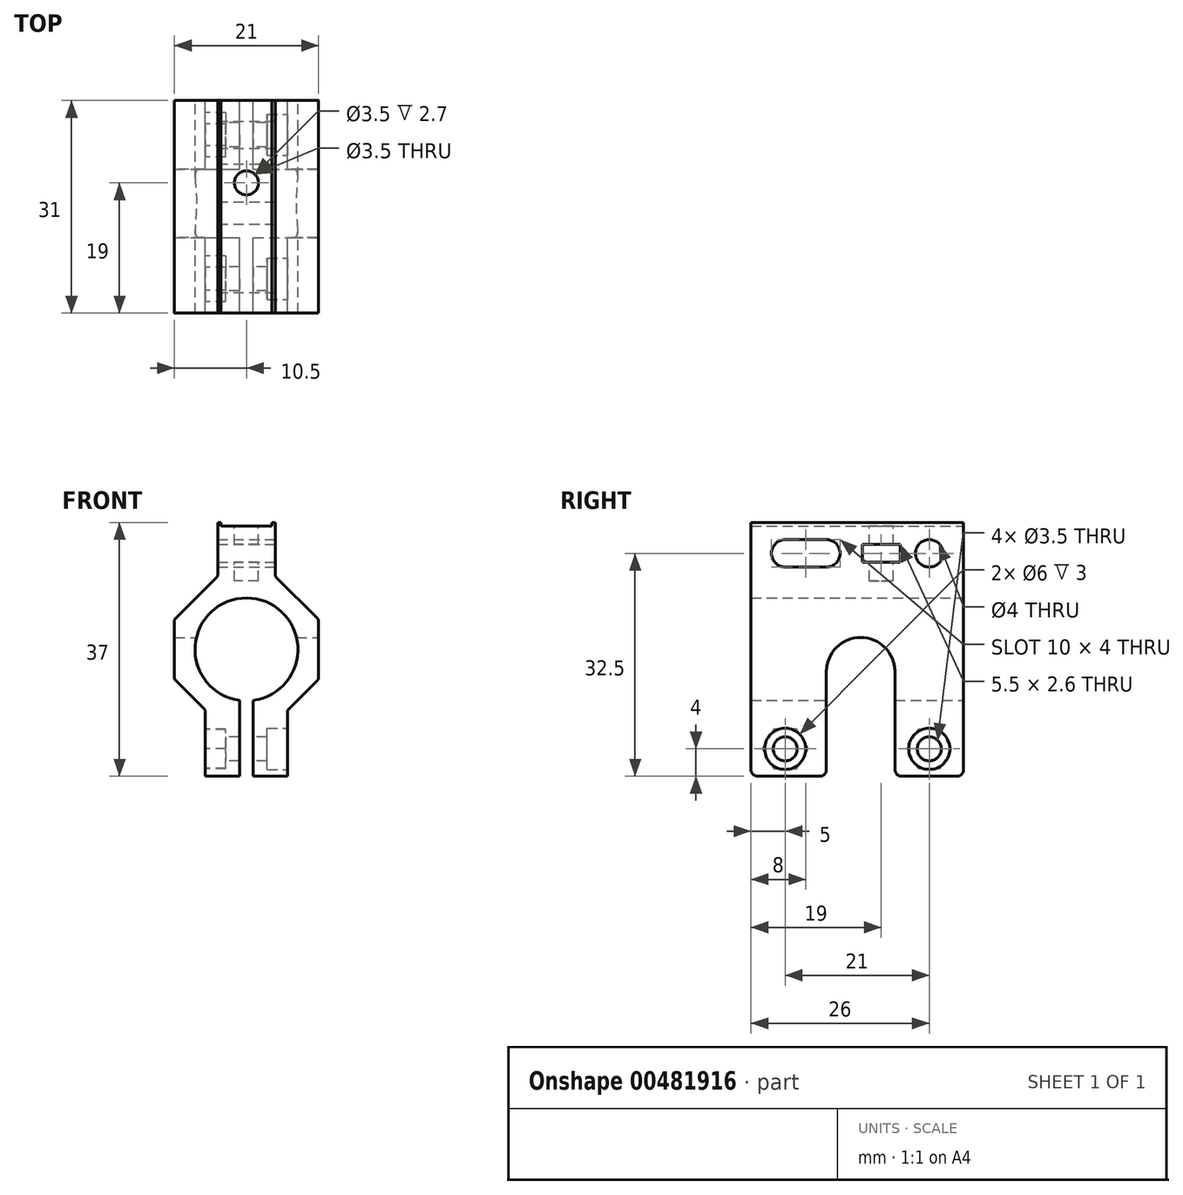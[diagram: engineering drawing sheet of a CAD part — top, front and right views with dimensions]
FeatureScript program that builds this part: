
annotation { "Feature Type Name" : "Feature", "Feature Type Description" : "" }
export const myFeature = defineFeature(function(context is Context, id is Id, definition is map)
    precondition{}
    {
        {
            var Q0;
            Q0=qCreatedBy(makeId("Front.planeOp"),FACE);
            var sketch = newSketch(context, id + "F0", { "sketchPlane" : qUnion([Q0])});
            skCircle(sketch, "E0", {"center": v(0, 0) * mm, "radius": 7.5 * mm});
            skCircle(sketch, "E1.cCircle", {"center": v(0, 0) * mm, "radius": 10.5 * mm, "construction": true});
            skLineSegment(sketch, "E1.1", {"start": v(4.2, 10.65) * mm, "end": v(10.5, 4.35) * mm});
            skLineSegment(sketch, "E1.2", {"start": v(10.5, 4.35) * mm, "end": v(10.5, -4.35) * mm});
            skLineSegment(sketch, "E1.3", {"start": v(10.5, -4.35) * mm, "end": v(6, -8.85) * mm});
            skLineSegment(sketch, "E1.5", {"start": v(-6, -8.85) * mm, "end": v(-10.5, -4.35) * mm});
            skLineSegment(sketch, "E1.6", {"start": v(-10.5, -4.35) * mm, "end": v(-10.5, 4.35) * mm});
            skLineSegment(sketch, "E1.7", {"start": v(-10.5, 4.35) * mm, "end": v(-4.2, 10.65) * mm});
            skPoint(sketch, "E1.0.midPoint", {"position": v(0, 10.5) * mm});
            skLineSegment(sketch, "E2.bottom", {"start": v(-3.7, 18) * mm, "end": v(3.7, 18) * mm});
            skLineSegment(sketch, "E2.left", {"start": v(-4.2, 18.5) * mm, "end": v(-4.2, 10.65) * mm});
            skLineSegment(sketch, "E2.right", {"start": v(4.2, 18.5) * mm, "end": v(4.2, 10.65) * mm});
            skLineSegment(sketch, "E3.top", {"start": v(-6, -18.5) * mm, "end": v(6, -18.5) * mm});
            skLineSegment(sketch, "E3.left", {"start": v(-6, -8.85) * mm, "end": v(-6, -18.5) * mm});
            skLineSegment(sketch, "E3.right", {"start": v(6, -8.85) * mm, "end": v(6, -18.5) * mm});
            skLineSegment(sketch, "E4", {"start": v(0, 0) * mm, "end": v(0, 19.36) * mm, "construction": true});
            skLineSegment(sketch, "E5", {"start": v(-3.7, 18) * mm, "end": v(-3.7, 18.5) * mm});
            skLineSegment(sketch, "E6", {"start": v(-3.7, 18.5) * mm, "end": v(-4.2, 18.5) * mm});
            skLineSegment(sketch, "E7", {"start": v(3.7, 18) * mm, "end": v(3.7, 18.5) * mm});
            skLineSegment(sketch, "E8", {"start": v(3.7, 18.5) * mm, "end": v(4.2, 18.5) * mm});
            skSolve(sketch);
        }
        {
            var Q0;
            Q0 = qSketchRegion(id + "F0", true);
            extrude(context, id + "F1", {"entities" : qUnion([Q0]), "depth" : 31 * mm, "offsetDistance" : 25 * mm});
        }
        {
            var Q0;
            Q0=qCreatedBy(makeId("Front.planeOp"),FACE);
            var sketch = newSketch(context, id + "F2", { "sketchPlane" : qUnion([Q0])});
            skLineSegment(sketch, "E9.bottom", {"start": v(-1, 0) * mm, "end": v(1, 0) * mm});
            skLineSegment(sketch, "E9.top", {"start": v(-1, -21.28) * mm, "end": v(1, -21.28) * mm});
            skLineSegment(sketch, "E9.left", {"start": v(-1, 0) * mm, "end": v(-1, -21.28) * mm});
            skLineSegment(sketch, "E9.right", {"start": v(1, 0) * mm, "end": v(1, -21.28) * mm});
            skSolve(sketch);
        }
        {
            var Q0;
            Q0 = qSketchRegion(id + "F2", true);
            extrude(context, id + "F3", {"entities" : qUnion([Q0]), "operationType" : NewBodyOperationType.REMOVE, "endBound" : BoundingType.THROUGH_ALL, "depth" : 25 * mm});
        }
        {
            var Q0;
            Q0=qCreatedBy(makeId("Right.planeOp"),FACE);
            var sketch = newSketch(context, id + "F4", { "sketchPlane" : qUnion([Q0])});
            skCircle(sketch, "E10", {"center": v(-5, 14) * mm, "radius": 2 * mm});
            skLineSegment(sketch, "E11.bottom", {"start": v(-20, 16) * mm, "end": v(-26, 16) * mm});
            skLineSegment(sketch, "E11.top", {"start": v(-20, 12) * mm, "end": v(-26, 12) * mm});
            skLineSegment(sketch, "E11.left", {"start": v(-18, 14) * mm, "end": v(-18, 14) * mm});
            skLineSegment(sketch, "E11.right", {"start": v(-28, 14) * mm, "end": v(-28, 14) * mm});
            skPoint(sketch, "E12.visualSharp", {"position": v(-18, 16) * mm});
            skArc(sketch, "E12.filletArc", {"start": v(-18, 14) * mm, "mid": v(-18.59, 15.41) * mm, "end": v(-20, 16) * mm});
            skPoint(sketch, "E13.visualSharp", {"position": v(-18, 12) * mm});
            skArc(sketch, "E13.filletArc", {"start": v(-20, 12) * mm, "mid": v(-18.59, 12.59) * mm, "end": v(-18, 14) * mm});
            skPoint(sketch, "E14.visualSharp", {"position": v(-28, 12) * mm});
            skArc(sketch, "E14.filletArc", {"start": v(-28, 14) * mm, "mid": v(-27.41, 12.59) * mm, "end": v(-26, 12) * mm});
            skPoint(sketch, "E15.visualSharp", {"position": v(-28, 16) * mm});
            skArc(sketch, "E15.filletArc", {"start": v(-26, 16) * mm, "mid": v(-27.41, 15.41) * mm, "end": v(-28, 14) * mm});
            skLineSegment(sketch, "E16", {"start": v(-20, 14) * mm, "end": v(-26, 14) * mm, "construction": true});
            skLineSegment(sketch, "E17.bottom", {"start": v(-9.25, 15.3) * mm, "end": v(-14.75, 15.3) * mm});
            skLineSegment(sketch, "E17.top", {"start": v(-9.25, 12.7) * mm, "end": v(-14.75, 12.7) * mm});
            skLineSegment(sketch, "E17.left", {"start": v(-9.25, 15.3) * mm, "end": v(-9.25, 12.7) * mm});
            skLineSegment(sketch, "E17.right", {"start": v(-14.75, 15.3) * mm, "end": v(-14.75, 12.7) * mm});
            skLineSegment(sketch, "E18", {"start": v(-12, 23.23) * mm, "end": v(-12, 11.82) * mm, "construction": true});
            skLineSegment(sketch, "E19", {"start": v(-15.7, 14) * mm, "end": v(-8.39, 14) * mm, "construction": true});
            skPoint(sketch, "E19.startSnap0", {"position": v(-14.75, 14) * mm});
            skSolve(sketch);
        }
        {
            var Q0;
            Q0 = qSketchRegion(id + "F4", true);
            extrude(context, id + "F5", {"entities" : qUnion([Q0]), "operationType" : NewBodyOperationType.REMOVE, "endBound" : BoundingType.SYMMETRIC, "oppositeDirection" : true, "depth" : 25 * mm});
        }
        {
            var Q0;
            Q0=qCreatedBy(makeId("Right.planeOp"),FACE);
            var sketch = newSketch(context, id + "F6", { "sketchPlane" : qUnion([Q0])});
            skLineSegment(sketch, "E20.bottom", {"start": v(-15, 1.74) * mm, "end": v(-15, 1.74) * mm});
            skLineSegment(sketch, "E20.top", {"start": v(-20, -23.5) * mm, "end": v(-10, -23.5) * mm});
            skLineSegment(sketch, "E20.left", {"start": v(-20, -3.26) * mm, "end": v(-20, -23.5) * mm});
            skLineSegment(sketch, "E20.right", {"start": v(-10, -3.26) * mm, "end": v(-10, -23.5) * mm});
            skPoint(sketch, "E21.visualSharp", {"position": v(-20, 1.74) * mm});
            skArc(sketch, "E21.filletArc", {"start": v(-15, 1.74) * mm, "mid": v(-18.54, 0.28) * mm, "end": v(-20, -3.26) * mm});
            skPoint(sketch, "E22.visualSharp", {"position": v(-10, 1.74) * mm});
            skArc(sketch, "E22.filletArc", {"start": v(-10, -3.26) * mm, "mid": v(-11.46, 0.28) * mm, "end": v(-15, 1.74) * mm});
            skSolve(sketch);
        }
        {
            var Q0;
            Q0 = qSketchRegion(id + "F6", true);
            extrude(context, id + "F7", {"entities" : qUnion([Q0]), "operationType" : NewBodyOperationType.REMOVE, "endBound" : BoundingType.SYMMETRIC, "oppositeDirection" : true, "depth" : 25 * mm});
        }
        {
            var Q0;
            Q0=makeQuery(id+"F1.opExtrude","CAP_EDGE",EDGE,{"disambiguationData":[OSD([sQuery(id+"F0.wireOp",EDGE,"E3.top")])],"isStart":true});
            var Q1;
            Q1=makeQuery(id+"F1.opExtrude","CAP_EDGE",EDGE,{"disambiguationData":[OSD([sQuery(id+"F0.wireOp",EDGE,"E3.top")])],"isStart":false});
            var Q2;
            {var subQ0=sQuery(id+"F0.wireOp",EDGE,"E3.right");var subQ2=sQuery(id+"F0.wireOp",EDGE,"E3.top");Q2=makeQuery(id+"F7.boolean.opBoolean","INTERSECT",EDGE,{"derivedFrom":[makeQuery(id+"F3.boolean.opBoolean","SPLIT",FACE,{"disambiguationData":[TD([makeQuery(id+"F1.opExtrude","SWEPT_FACE",FACE,{"disambiguationData":[OSD([subQ0])]})])],"derivedFrom":makeQuery(id+"F1.opExtrude","SWEPT_FACE",FACE,{"disambiguationData":[OSD([subQ2])]})}),makeQuery(id+"F7.opExtrude","SWEPT_FACE",FACE,{"disambiguationData":[OSD([sQuery(id+"F6.wireOp",EDGE,"E20.left")])]})]});}
            var Q3;
            {var subQ1=sQuery(id+"F0.wireOp",EDGE,"E3.left");var subQ2=sQuery(id+"F0.wireOp",EDGE,"E3.top");Q3=makeQuery(id+"F7.boolean.opBoolean","INTERSECT",EDGE,{"derivedFrom":[makeQuery(id+"F3.boolean.opBoolean","SPLIT",FACE,{"disambiguationData":[TD([makeQuery(id+"F1.opExtrude","SWEPT_FACE",FACE,{"disambiguationData":[OSD([subQ1])]})])],"derivedFrom":makeQuery(id+"F1.opExtrude","SWEPT_FACE",FACE,{"disambiguationData":[OSD([subQ2])]})}),makeQuery(id+"F7.opExtrude","SWEPT_FACE",FACE,{"disambiguationData":[OSD([sQuery(id+"F6.wireOp",EDGE,"E20.left")])]})]});}
            var Q4;
            {var subQ0=sQuery(id+"F0.wireOp",EDGE,"E3.right");var subQ2=sQuery(id+"F0.wireOp",EDGE,"E3.top");Q4=makeQuery(id+"F7.boolean.opBoolean","INTERSECT",EDGE,{"derivedFrom":[makeQuery(id+"F3.boolean.opBoolean","SPLIT",FACE,{"disambiguationData":[TD([makeQuery(id+"F1.opExtrude","SWEPT_FACE",FACE,{"disambiguationData":[OSD([subQ0])]})])],"derivedFrom":makeQuery(id+"F1.opExtrude","SWEPT_FACE",FACE,{"disambiguationData":[OSD([subQ2])]})}),makeQuery(id+"F7.opExtrude","SWEPT_FACE",FACE,{"disambiguationData":[OSD([sQuery(id+"F6.wireOp",EDGE,"E20.right")])]})]});}
            var Q5;
            {var subQ1=sQuery(id+"F0.wireOp",EDGE,"E3.left");var subQ2=sQuery(id+"F0.wireOp",EDGE,"E3.top");Q5=makeQuery(id+"F7.boolean.opBoolean","INTERSECT",EDGE,{"derivedFrom":[makeQuery(id+"F3.boolean.opBoolean","SPLIT",FACE,{"disambiguationData":[TD([makeQuery(id+"F1.opExtrude","SWEPT_FACE",FACE,{"disambiguationData":[OSD([subQ1])]})])],"derivedFrom":makeQuery(id+"F1.opExtrude","SWEPT_FACE",FACE,{"disambiguationData":[OSD([subQ2])]})}),makeQuery(id+"F7.opExtrude","SWEPT_FACE",FACE,{"disambiguationData":[OSD([sQuery(id+"F6.wireOp",EDGE,"E20.right")])]})]});}
            fillet(context, id + "F8", {"entities" : qUnion([Q0, Q1, Q2, Q3, Q4, Q5]), "radius" : 1 * mm, "tangentPropagation" : true, "allowEdgeOverflow" : false});
        }
        {
            var Q0;
            Q0=makeQuery(id+"F1.opExtrude","SWEPT_EDGE",EDGE,{"disambiguationData":[OSD([sQuery(id+"F0.wireOp",EDGE,"E1.7"),sQuery(id+"F0.wireOp",EDGE,"E2.left")])]});
            var Q1;
            {var subQ0=sQuery(id+"F0.wireOp",EDGE,"E3.right");var subQ1=sQuery(id+"F0.wireOp",EDGE,"E1.3");Q1=makeQuery(id+"F7.boolean.opBoolean","SPLIT",EDGE,{"disambiguationData":[TD([makeQuery(id+"F7.opExtrude","SWEPT_FACE",FACE,{"disambiguationData":[OSD([sQuery(id+"F6.wireOp",EDGE,"E20.left")])]})])],"derivedFrom":makeQuery(id+"F1.opExtrude","SWEPT_EDGE",EDGE,{"disambiguationData":[OSD([subQ1,subQ0])]})});}
            var Q2;
            {var subQ0=sQuery(id+"F0.wireOp",EDGE,"E3.right");var subQ1=sQuery(id+"F0.wireOp",EDGE,"E1.3");Q2=makeQuery(id+"F7.boolean.opBoolean","SPLIT",EDGE,{"disambiguationData":[TD([makeQuery(id+"F7.opExtrude","SWEPT_FACE",FACE,{"disambiguationData":[OSD([sQuery(id+"F6.wireOp",EDGE,"E20.right")])]})])],"derivedFrom":makeQuery(id+"F1.opExtrude","SWEPT_EDGE",EDGE,{"disambiguationData":[OSD([subQ1,subQ0])]})});}
            var Q3;
            {var subQ0=sQuery(id+"F0.wireOp",EDGE,"E1.3");var subQ1=sQuery(id+"F0.wireOp",EDGE,"E1.2");Q3=makeQuery(id+"F7.boolean.opBoolean","SPLIT",EDGE,{"disambiguationData":[TD([makeQuery(id+"F7.opExtrude","SWEPT_FACE",FACE,{"disambiguationData":[OSD([sQuery(id+"F6.wireOp",EDGE,"E20.right")])]})])],"derivedFrom":makeQuery(id+"F1.opExtrude","SWEPT_EDGE",EDGE,{"disambiguationData":[OSD([subQ1,subQ0])]})});}
            var Q4;
            {var subQ0=sQuery(id+"F0.wireOp",EDGE,"E1.3");var subQ1=sQuery(id+"F0.wireOp",EDGE,"E1.2");Q4=makeQuery(id+"F7.boolean.opBoolean","SPLIT",EDGE,{"disambiguationData":[TD([makeQuery(id+"F7.opExtrude","SWEPT_FACE",FACE,{"disambiguationData":[OSD([sQuery(id+"F6.wireOp",EDGE,"E20.left")])]})])],"derivedFrom":makeQuery(id+"F1.opExtrude","SWEPT_EDGE",EDGE,{"disambiguationData":[OSD([subQ1,subQ0])]})});}
            var Q5;
            Q5=makeQuery(id+"F1.opExtrude","SWEPT_EDGE",EDGE,{"disambiguationData":[OSD([sQuery(id+"F0.wireOp",EDGE,"E1.1"),sQuery(id+"F0.wireOp",EDGE,"E1.2")])]});
            var Q6;
            Q6=makeQuery(id+"F1.opExtrude","SWEPT_EDGE",EDGE,{"disambiguationData":[OSD([sQuery(id+"F0.wireOp",EDGE,"E1.1"),sQuery(id+"F0.wireOp",EDGE,"E2.right")])]});
            var Q7;
            Q7=makeQuery(id+"F1.opExtrude","SWEPT_EDGE",EDGE,{"disambiguationData":[OSD([sQuery(id+"F0.wireOp",EDGE,"E1.6"),sQuery(id+"F0.wireOp",EDGE,"E1.7")])]});
            var Q8;
            {var subQ0=sQuery(id+"F0.wireOp",EDGE,"E1.6");var subQ1=sQuery(id+"F0.wireOp",EDGE,"E1.5");Q8=makeQuery(id+"F7.boolean.opBoolean","SPLIT",EDGE,{"disambiguationData":[TD([makeQuery(id+"F7.opExtrude","SWEPT_FACE",FACE,{"disambiguationData":[OSD([sQuery(id+"F6.wireOp",EDGE,"E20.left")])]})])],"derivedFrom":makeQuery(id+"F1.opExtrude","SWEPT_EDGE",EDGE,{"disambiguationData":[OSD([subQ1,subQ0])]})});}
            var Q9;
            {var subQ0=sQuery(id+"F0.wireOp",EDGE,"E1.6");var subQ1=sQuery(id+"F0.wireOp",EDGE,"E1.5");Q9=makeQuery(id+"F7.boolean.opBoolean","SPLIT",EDGE,{"disambiguationData":[TD([makeQuery(id+"F7.opExtrude","SWEPT_FACE",FACE,{"disambiguationData":[OSD([sQuery(id+"F6.wireOp",EDGE,"E20.right")])]})])],"derivedFrom":makeQuery(id+"F1.opExtrude","SWEPT_EDGE",EDGE,{"disambiguationData":[OSD([subQ1,subQ0])]})});}
            var Q10;
            {var subQ0=sQuery(id+"F0.wireOp",EDGE,"E3.left");var subQ1=sQuery(id+"F0.wireOp",EDGE,"E1.5");Q10=makeQuery(id+"F7.boolean.opBoolean","SPLIT",EDGE,{"disambiguationData":[TD([makeQuery(id+"F7.opExtrude","SWEPT_FACE",FACE,{"disambiguationData":[OSD([sQuery(id+"F6.wireOp",EDGE,"E20.right")])]})])],"derivedFrom":makeQuery(id+"F1.opExtrude","SWEPT_EDGE",EDGE,{"disambiguationData":[OSD([subQ1,subQ0])]})});}
            var Q11;
            {var subQ0=sQuery(id+"F0.wireOp",EDGE,"E3.left");var subQ1=sQuery(id+"F0.wireOp",EDGE,"E1.5");Q11=makeQuery(id+"F7.boolean.opBoolean","SPLIT",EDGE,{"disambiguationData":[TD([makeQuery(id+"F7.opExtrude","SWEPT_FACE",FACE,{"disambiguationData":[OSD([sQuery(id+"F6.wireOp",EDGE,"E20.left")])]})])],"derivedFrom":makeQuery(id+"F1.opExtrude","SWEPT_EDGE",EDGE,{"disambiguationData":[OSD([subQ1,subQ0])]})});}
            fillet(context, id + "F9", {"entities" : qUnion([Q0, Q1, Q2, Q3, Q4, Q5, Q6, Q7, Q8, Q9, Q10, Q11]), "radius" : .5 * mm, "tangentPropagation" : true, "allowEdgeOverflow" : false});
        }
        {
            var Q0;
            Q0=qCreatedBy(makeId("Right.planeOp"),FACE);
            var sketch = newSketch(context, id + "F10", { "sketchPlane" : qUnion([Q0])});
            skCircle(sketch, "E23", {"center": v(-26, -14.5) * mm, "radius": 1.75 * mm});
            skCircle(sketch, "E24", {"center": v(-5, -14.5) * mm, "radius": 1.75 * mm});
            skSolve(sketch);
        }
        {
            var Q0;
            Q0 = qSketchRegion(id + "F10", true);
            extrude(context, id + "F11", {"entities" : qUnion([Q0]), "operationType" : NewBodyOperationType.REMOVE, "endBound" : BoundingType.SYMMETRIC, "depth" : 25 * mm});
        }
        {
            var Q0;
            {var subQ0=sQuery(id+"F0.wireOp",EDGE,"E3.right");Q0=makeQuery(id+"F7.boolean.opBoolean","SPLIT",FACE,{"disambiguationData":[TD([makeQuery(id+"F7.opExtrude","SWEPT_FACE",FACE,{"disambiguationData":[OSD([sQuery(id+"F6.wireOp",EDGE,"E20.right")])]})])],"derivedFrom":makeQuery(id+"F1.opExtrude","SWEPT_FACE",FACE,{"disambiguationData":[OSD([subQ0])]})});}
            var sketch = newSketch(context, id + "F12", { "sketchPlane" : qUnion([Q0])});
            skCircle(sketch, "E25", {"center": v(-5, -14.5) * mm, "radius": 3 * mm});
            skCircle(sketch, "E26", {"center": v(-26, -14.5) * mm, "radius": 3 * mm});
            skSolve(sketch);
        }
        {
            var Q0;
            Q0 = qSketchRegion(id + "F12", true);
            extrude(context, id + "F13", {"entities" : qUnion([Q0]), "operationType" : NewBodyOperationType.REMOVE, "oppositeDirection" : true, "depth" : 3 * mm, "offsetDistance" : 25 * mm});
        }
        {
            var Q0;
            {var subQ1=sQuery(id+"F0.wireOp",EDGE,"E3.left");Q0=makeQuery(id+"F7.boolean.opBoolean","SPLIT",FACE,{"disambiguationData":[TD([makeQuery(id+"F7.opExtrude","SWEPT_FACE",FACE,{"disambiguationData":[OSD([sQuery(id+"F6.wireOp",EDGE,"E20.left")])]})])],"derivedFrom":makeQuery(id+"F1.opExtrude","SWEPT_FACE",FACE,{"disambiguationData":[OSD([subQ1])]})});}
            var sketch = newSketch(context, id + "F14", { "sketchPlane" : qUnion([Q0])});
            skCircle(sketch, "E27.cCircle", {"center": v(26, -14.5) * mm, "radius": 2.9 * mm, "construction": true});
            skLineSegment(sketch, "E27.0", {"start": v(24.33, -11.6) * mm, "end": v(27.67, -11.6) * mm});
            skLineSegment(sketch, "E27.1", {"start": v(27.67, -11.6) * mm, "end": v(29.35, -14.5) * mm});
            skLineSegment(sketch, "E27.2", {"start": v(29.35, -14.5) * mm, "end": v(27.67, -17.4) * mm});
            skLineSegment(sketch, "E27.3", {"start": v(27.67, -17.4) * mm, "end": v(24.33, -17.4) * mm});
            skLineSegment(sketch, "E27.4", {"start": v(24.33, -17.4) * mm, "end": v(22.65, -14.5) * mm});
            skLineSegment(sketch, "E27.5", {"start": v(22.65, -14.5) * mm, "end": v(24.33, -11.6) * mm});
            skPoint(sketch, "E27.0.midPoint", {"position": v(26, -11.6) * mm});
            skCircle(sketch, "E28.cCircle", {"center": v(5, -14.5) * mm, "radius": 2.8 * mm, "construction": true});
            skLineSegment(sketch, "E28.0", {"start": v(3.38, -11.7) * mm, "end": v(6.62, -11.7) * mm});
            skLineSegment(sketch, "E28.1", {"start": v(6.62, -11.7) * mm, "end": v(8.23, -14.5) * mm});
            skLineSegment(sketch, "E28.2", {"start": v(8.23, -14.5) * mm, "end": v(6.62, -17.3) * mm});
            skLineSegment(sketch, "E28.3", {"start": v(6.62, -17.3) * mm, "end": v(3.38, -17.3) * mm});
            skLineSegment(sketch, "E28.4", {"start": v(3.38, -17.3) * mm, "end": v(1.77, -14.5) * mm});
            skLineSegment(sketch, "E28.5", {"start": v(1.77, -14.5) * mm, "end": v(3.38, -11.7) * mm});
            skPoint(sketch, "E28.0.midPoint", {"position": v(5, -11.7) * mm});
            skSolve(sketch);
        }
        {
            var Q0;
            Q0 = qSketchRegion(id + "F14", true);
            extrude(context, id + "F15", {"entities" : qUnion([Q0]), "operationType" : NewBodyOperationType.REMOVE, "oppositeDirection" : true, "depth" : 3 * mm, "offsetDistance" : 25 * mm});
        }
        {
            var Q0;
            Q0=makeQuery(id+"F1.opExtrude","SWEPT_FACE",FACE,{"disambiguationData":[OSD([sQuery(id+"F0.wireOp",EDGE,"E2.bottom")])]});
            var sketch = newSketch(context, id + "F16", { "sketchPlane" : qUnion([Q0])});
            skCircle(sketch, "E29", {"center": v(0, -12) * mm, "radius": 1.75 * mm});
            skSolve(sketch);
        }
        {
            var Q0;
            Q0 = qSketchRegion(id + "F16", true);
            extrude(context, id + "F17", {"entities" : qUnion([Q0]), "operationType" : NewBodyOperationType.REMOVE, "oppositeDirection" : true, "depth" : 8 * mm, "offsetDistance" : 25 * mm});
        }
    });
